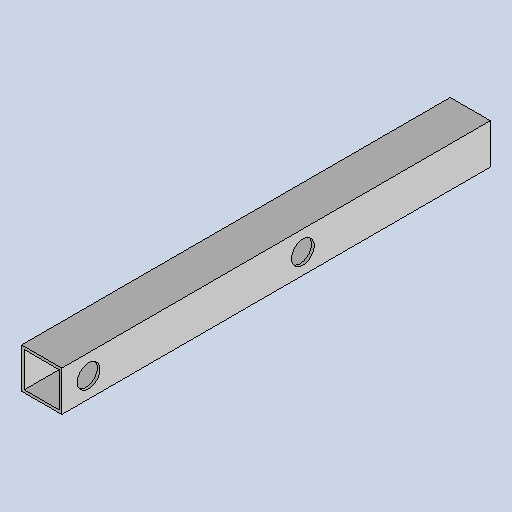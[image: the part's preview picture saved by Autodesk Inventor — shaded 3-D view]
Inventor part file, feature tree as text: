
AUTODESK INVENTOR PART (.ipt)
format: ipt  version: 2025.1 (Build 291241020, 241B)  size: 148,992 bytes
history: native  units: mm
features: extrude x2, sketch x2, projected_geometry x1
ambient origin geometry x8: Origin, YZ Plane, XZ Plane, XY Plane, X Axis, Y Axis, Z Axis, Center Point
bodies: Body1 (feature_tree)
feature tree (5):
  extrude  "Extrusion3"  Depth=30.0mm
  extrude  "Extrusion4"  Depth=2.0mm
  sketch  "Sketch9"  dims[d61=500.0mm d172=30.0mm]
  sketch  "Sketch10"  dims[d173=30.0mm d174=2.0mm d175=320.0mm d176=0.0mm d177=17.0mm d178=17.0mm d179=0.0mm d180=0.0mm d181=30.0mm d182=170.0mm d183=330.0mm d184=450.0mm d185=500.0mm d186=17.0mm]
  projected_geometry  "Projected Loop3"
